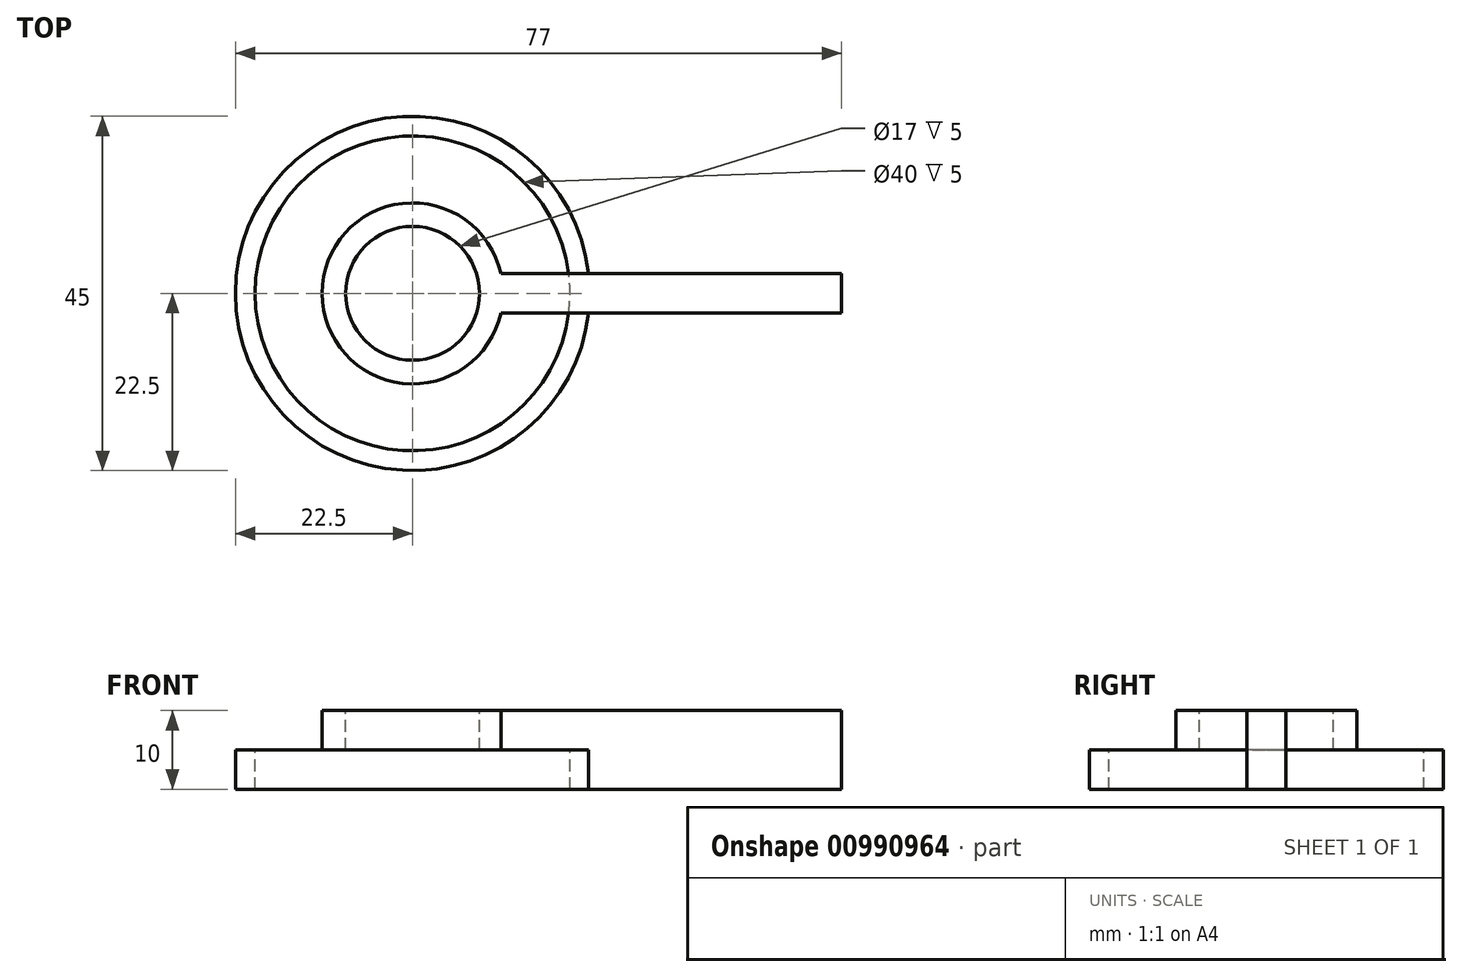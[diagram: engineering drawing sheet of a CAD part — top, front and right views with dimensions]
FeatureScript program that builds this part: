
annotation { "Feature Type Name" : "Feature", "Feature Type Description" : "" }
export const myFeature = defineFeature(function(context is Context, id is Id, definition is map)
    precondition{}
    {
        {
            var Q0;
            Q0=qCreatedBy(makeId("Top.planeOp"),FACE);
            var sketch = newSketch(context, id + "F0", { "sketchPlane" : qUnion([Q0])});
            skCircle(sketch, "E0", {"center": v(0, 0) * mm, "radius": 8.5 * mm});
            skCircle(sketch, "E1", {"center": v(0, 0) * mm, "radius": 11.5 * mm});
            skLineSegment(sketch, "E2", {"start": v(0, 0) * mm, "end": v(38.92, 0) * mm, "construction": true});
            skLineSegment(sketch, "E3", {"start": v(54.5, 0) * mm, "end": v(54.5, 2.5) * mm});
            skLineSegment(sketch, "E4", {"start": v(54.5, 2.5) * mm, "end": v(11.22, 2.5) * mm});
            skLineSegment(sketch, "E5.MirrorCS", {"start": v(54.5, 0) * mm, "end": v(54.5, -2.5) * mm});
            skLineSegment(sketch, "E6.MirrorCS", {"start": v(54.5, -2.5) * mm, "end": v(11.22, -2.5) * mm});
            skPoint(sketch, "E7", {"position": v(11.5, 0) * mm});
            skSolve(sketch);
        }
        {
            var Q0;
            Q0=makeQuery(id+"F0.imprint","IMPRINT",FACE,{"disambiguationData":[TD([[makeQuery(id+"F0.imprint","IMPRINT",EDGE,{"derivedFrom":sQuery(id+"F0.wireOp",EDGE,"E3")}),1.0]])]});
            var Q1;
            Q1=makeQuery(id+"F0.imprint","IMPRINT",FACE,{"disambiguationData":[TD([[makeQuery(id+"F0.imprint","IMPRINT",EDGE,{"derivedFrom":sQuery(id+"F0.wireOp",EDGE,"E0")}),-1.0]])]});
            extrude(context, id + "F1", {"entities" : qUnion([Q0, Q1]), "oppositeDirection" : true, "depth" : 5 * mm, "offsetDistance" : 25 * mm});
        }
        {
            var Q0;
            Q0=makeQuery(id+"F1.opExtrude","CAP_FACE",FACE,{"disambiguationData":[OSD([sQuery(id+"F0.wireOp",EDGE,"E0"),sQuery(id+"F0.wireOp",EDGE,"E1"),sQuery(id+"F0.wireOp",EDGE,"E3"),sQuery(id+"F0.wireOp",EDGE,"E4"),sQuery(id+"F0.wireOp",EDGE,"E5.MirrorCS"),sQuery(id+"F0.wireOp",EDGE,"E6.MirrorCS")])],"isStart":false});
            var sketch = newSketch(context, id + "F2", { "sketchPlane" : qUnion([Q0])});
            skCircle(sketch, "E8", {"center": v(0, 0) * mm, "radius": 20 * mm});
            skCircle(sketch, "E9", {"center": v(0, 0) * mm, "radius": 22.5 * mm});
            skSolve(sketch);
        }
        {
            var Q0;
            {var subQ5=makeQuery(id+"F1.opExtrude","CAP_EDGE",EDGE,{"disambiguationData":[OSD([sQuery(id+"F0.wireOp",EDGE,"E3"),sQuery(id+"F0.wireOp",EDGE,"E5.MirrorCS")])],"isStart":false});Q0=makeQuery(id+"F2.imprint","IMPRINT",FACE,{"disambiguationData":[TD([[makeQuery(id+"F2.imprint","IMPRINT",EDGE,{"derivedFrom":subQ5}),1.0]])]});}
            var Q1;
            {var subQ0=sQuery(id+"F2.wireOp",EDGE,"E8");var subQ1=makeQuery(id+"F1.opExtrude","CAP_EDGE",EDGE,{"disambiguationData":[OSD([sQuery(id+"F0.wireOp",EDGE,"E4")])],"isStart":false});var subQ2=makeQuery(id+"F2.imprint","INTERSECT",VERTEX,{"derivedFrom":[subQ1,subQ0]});Q1=makeQuery(id+"F2.imprint","IMPRINT",FACE,{"disambiguationData":[TD([[makeQuery(id+"F2.imprint","IMPRINT",EDGE,{"disambiguationData":[TD([[subQ2,1.0]])],"derivedFrom":subQ0}),-1.0]])]});}
            var Q2;
            {var subQ0=sQuery(id+"F2.wireOp",EDGE,"E8");var subQ1=makeQuery(id+"F1.opExtrude","CAP_EDGE",EDGE,{"disambiguationData":[OSD([sQuery(id+"F0.wireOp",EDGE,"E4")])],"isStart":false});var subQ2=makeQuery(id+"F2.imprint","INTERSECT",VERTEX,{"derivedFrom":[subQ1,subQ0]});Q2=makeQuery(id+"F2.imprint","IMPRINT",FACE,{"disambiguationData":[TD([[makeQuery(id+"F2.imprint","IMPRINT",EDGE,{"disambiguationData":[TD([[subQ2,-1.0]])],"derivedFrom":subQ0}),-1.0]])]});}
            extrude(context, id + "F3", {"entities" : qUnion([Q0, Q1, Q2]), "operationType" : NewBodyOperationType.ADD, "depth" : 5 * mm, "offsetDistance" : 25 * mm});
        }
    });
